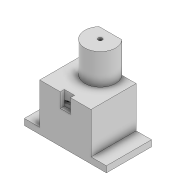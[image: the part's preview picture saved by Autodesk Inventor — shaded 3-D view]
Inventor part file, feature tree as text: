
AUTODESK INVENTOR PART (.ipt)
format: ipt  version: 2022 (Build 260153000, 153)  size: 182,784 bytes
history: native  units: mm
features: extrude x8, sketch x8, projected_geometry x2, thicken_offset x1
ambient origin geometry x8: Origin, YZ Plane, XZ Plane, XY Plane, X Axis, Y Axis, Z Axis, Center Point
bodies: Solid1 (feature_tree)
feature tree (19):
  extrude  "Extrusion1"  Depth=25.0mm
  extrude  "Extrusion2"  Depth=20.0mm TaperAngle=0.0deg
  extrude  "Extrusion3"  Depth=100.0mm TaperAngle=0.0deg
  extrude  "Extrusion4"  Depth=15.0mm TaperAngle=0.0deg
  thicken_offset  "Thicken1"
  extrude  "Extrusion5"  Depth=40.0mm
  extrude  "Extrusion6"  Depth=3.0mm
  extrude  "Extrusion7"  Depth=10.0mm
  extrude  "Extrusion8"  Depth=3.0mm TaperAngle=0.0deg
  sketch  "Sketch1"  dims[d0=12.2mm d1=25.0mm]
  sketch  "Sketch2"  dims[d2=20.0mm d3=20.0mm d4=0.0mm]
  sketch  "Sketch3"  dims[d5=2.0mm d6=100.0mm d7=0.0mm]
  projected_geometry  "Projected Loop1"
  sketch  "Sketch4"  dims[d8=15.0mm d9=15.0mm d10=0.0mm]
  sketch  "Sketch5"  dims[d11=30.0mm d12=40.0mm]
  projected_geometry  "Projected Loop2"
  sketch  "Sketch6"  dims[d13=3.0mm d14=0.0mm d15=5.0mm]
  sketch  "Sketch7"  dims[d16=5.0mm d17=10.0mm]
  sketch  "Sketch8"  dims[d18=10.0mm d19=2.0mm d20=0.0mm d21=10.0mm d22=0.0mm d23=9.8mm d24=22.0mm d25=0.0mm d26=100.0mm d27=0.0mm d28=3.0mm]
